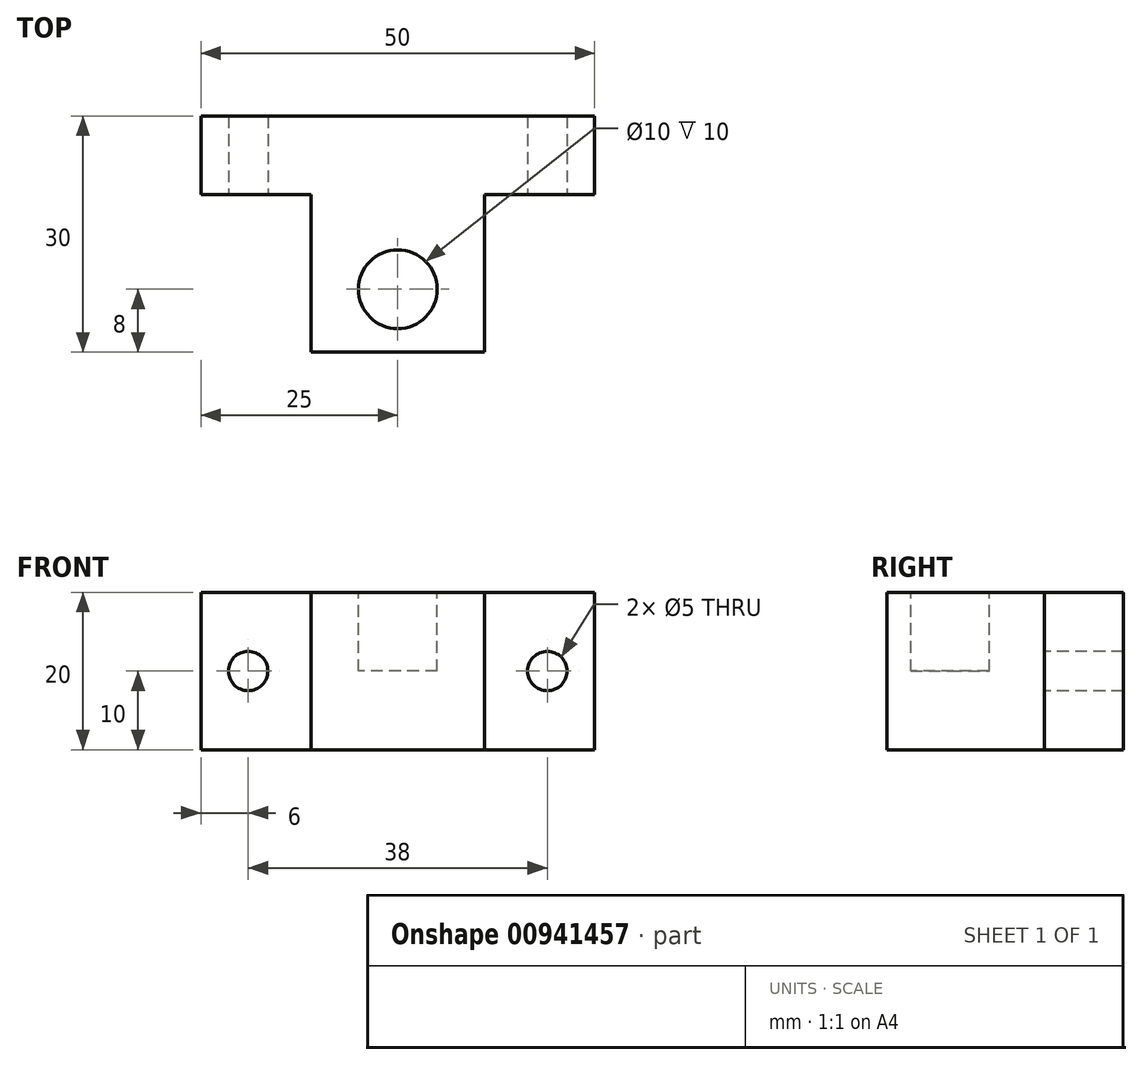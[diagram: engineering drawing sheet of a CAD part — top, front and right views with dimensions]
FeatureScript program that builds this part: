
annotation { "Feature Type Name" : "Feature", "Feature Type Description" : "" }
export const myFeature = defineFeature(function(context is Context, id is Id, definition is map)
    precondition{}
    {
        {
            var Q0;
            Q0=qCreatedBy(makeId("Front.planeOp"),FACE);
            var sketch = newSketch(context, id + "F0", { "sketchPlane" : qUnion([Q0])});
            skLineSegment(sketch, "E0.bottom", {"start": v(25, -10) * mm, "end": v(-25, -10) * mm});
            skLineSegment(sketch, "E0.top", {"start": v(25, 10) * mm, "end": v(-25, 10) * mm});
            skLineSegment(sketch, "E0.left", {"start": v(25, -10) * mm, "end": v(25, 10) * mm});
            skLineSegment(sketch, "E0.right", {"start": v(-25, -10) * mm, "end": v(-25, 10) * mm});
            skPoint(sketch, "E0.middle", {"position": v(0, 0) * mm});
            skSolve(sketch);
        }
        {
            var Q0;
            Q0=makeQuery(id+"F0.imprint","IMPRINT",FACE,{"disambiguationData":[TD([[makeQuery(id+"F0.imprint","IMPRINT",EDGE,{"derivedFrom":sQuery(id+"F0.wireOp",EDGE,"E0.bottom")}),-1.0]])]});
            extrude(context, id + "F1", {"entities" : qUnion([Q0]), "depth" : 30 * mm, "offsetDistance" : 25 * mm});
        }
        {
            var Q0;
            Q0=makeQuery(id+"F1.opExtrude","CAP_FACE",FACE,{"disambiguationData":[OSD([sQuery(id+"F0.wireOp",EDGE,"E0.bottom"),sQuery(id+"F0.wireOp",EDGE,"E0.top"),sQuery(id+"F0.wireOp",EDGE,"E0.left"),sQuery(id+"F0.wireOp",EDGE,"E0.right")])],"isStart":false});
            var sketch = newSketch(context, id + "F2", { "sketchPlane" : qUnion([Q0])});
            skLineSegment(sketch, "E1.bottom", {"start": v(-25, 10) * mm, "end": v(-11, 10) * mm});
            skLineSegment(sketch, "E1.top", {"start": v(-25, -10) * mm, "end": v(-11, -10) * mm});
            skLineSegment(sketch, "E1.left", {"start": v(-25, 10) * mm, "end": v(-25, -10) * mm});
            skLineSegment(sketch, "E1.right", {"start": v(-11, 10) * mm, "end": v(-11, -10) * mm});
            skLineSegment(sketch, "E2.bottom", {"start": v(25, 10) * mm, "end": v(11, 10) * mm});
            skLineSegment(sketch, "E2.top", {"start": v(25, -10) * mm, "end": v(11, -10) * mm});
            skLineSegment(sketch, "E2.left", {"start": v(25, 10) * mm, "end": v(25, -10) * mm});
            skLineSegment(sketch, "E2.right", {"start": v(11, 10) * mm, "end": v(11, -10) * mm});
            skSolve(sketch);
        }
        {
            var Q0;
            Q0=makeQuery(id+"F2.imprint","IMPRINT",FACE,{"disambiguationData":[TD([[makeQuery(id+"F2.imprint","IMPRINT",EDGE,{"derivedFrom":sQuery(id+"F2.wireOp",EDGE,"E1.bottom")}),1.0]])]});
            var Q1;
            Q1=makeQuery(id+"F2.imprint","IMPRINT",FACE,{"disambiguationData":[TD([[makeQuery(id+"F2.imprint","IMPRINT",EDGE,{"derivedFrom":sQuery(id+"F2.wireOp",EDGE,"E2.bottom")}),1.0]])]});
            extrude(context, id + "F3", {"entities" : qUnion([Q0, Q1]), "operationType" : NewBodyOperationType.REMOVE, "oppositeDirection" : true, "depth" : 20 * mm, "offsetDistance" : 25 * mm});
        }
        {
            var Q0;
            Q0=makeQuery(id+"F1.opExtrude","SWEPT_FACE",FACE,{"disambiguationData":[OSD([sQuery(id+"F0.wireOp",EDGE,"E0.top")])]});
            var sketch = newSketch(context, id + "F4", { "sketchPlane" : qUnion([Q0])});
            skCircle(sketch, "E3", {"center": v(0, -22) * mm, "radius": 5 * mm});
            skSolve(sketch);
        }
        {
            var Q0;
            Q0=makeQuery(id+"F4.imprint","IMPRINT",FACE,{"disambiguationData":[TD([[makeQuery(id+"F4.imprint","IMPRINT",EDGE,{"derivedFrom":sQuery(id+"F4.wireOp",EDGE,"E3")}),1.0]])]});
            extrude(context, id + "F5", {"entities" : qUnion([Q0]), "operationType" : NewBodyOperationType.REMOVE, "oppositeDirection" : true, "depth" : 10 * mm, "offsetDistance" : 25 * mm});
        }
        {
            var Q0;
            Q0=makeQuery(id+"F3.boolean.opBoolean","COPY",FACE,{"derivedFrom":makeQuery(id+"F3.opExtrude","CAP_FACE",FACE,{"disambiguationData":[OSD([sQuery(id+"F2.wireOp",EDGE,"E1.bottom"),sQuery(id+"F2.wireOp",EDGE,"E1.top"),sQuery(id+"F2.wireOp",EDGE,"E1.left"),sQuery(id+"F2.wireOp",EDGE,"E1.right")])],"isStart":false})});
            var sketch = newSketch(context, id + "F6", { "sketchPlane" : qUnion([Q0])});
            skCircle(sketch, "E4", {"center": v(-19, 0) * mm, "radius": 2.5 * mm});
            skPoint(sketch, "E4.centerSnap0", {"position": v(-25, 0) * mm});
            skCircle(sketch, "E5", {"center": v(19, 0) * mm, "radius": 2.5 * mm});
            skSolve(sketch);
        }
        {
            var Q0;
            Q0=makeQuery(id+"F6.imprint","IMPRINT",FACE,{"disambiguationData":[TD([[makeQuery(id+"F6.imprint","IMPRINT",EDGE,{"derivedFrom":sQuery(id+"F6.wireOp",EDGE,"E4")}),1.0]])]});
            var Q1;
            Q1=makeQuery(id+"F6.imprint","IMPRINT",FACE,{"disambiguationData":[TD([[makeQuery(id+"F6.imprint","IMPRINT",EDGE,{"derivedFrom":sQuery(id+"F6.wireOp",EDGE,"E5")}),1.0]])]});
            extrude(context, id + "F7", {"entities" : qUnion([Q0, Q1]), "operationType" : NewBodyOperationType.REMOVE, "oppositeDirection" : true, "depth" : 25 * mm, "offsetDistance" : 25 * mm});
        }
    });
